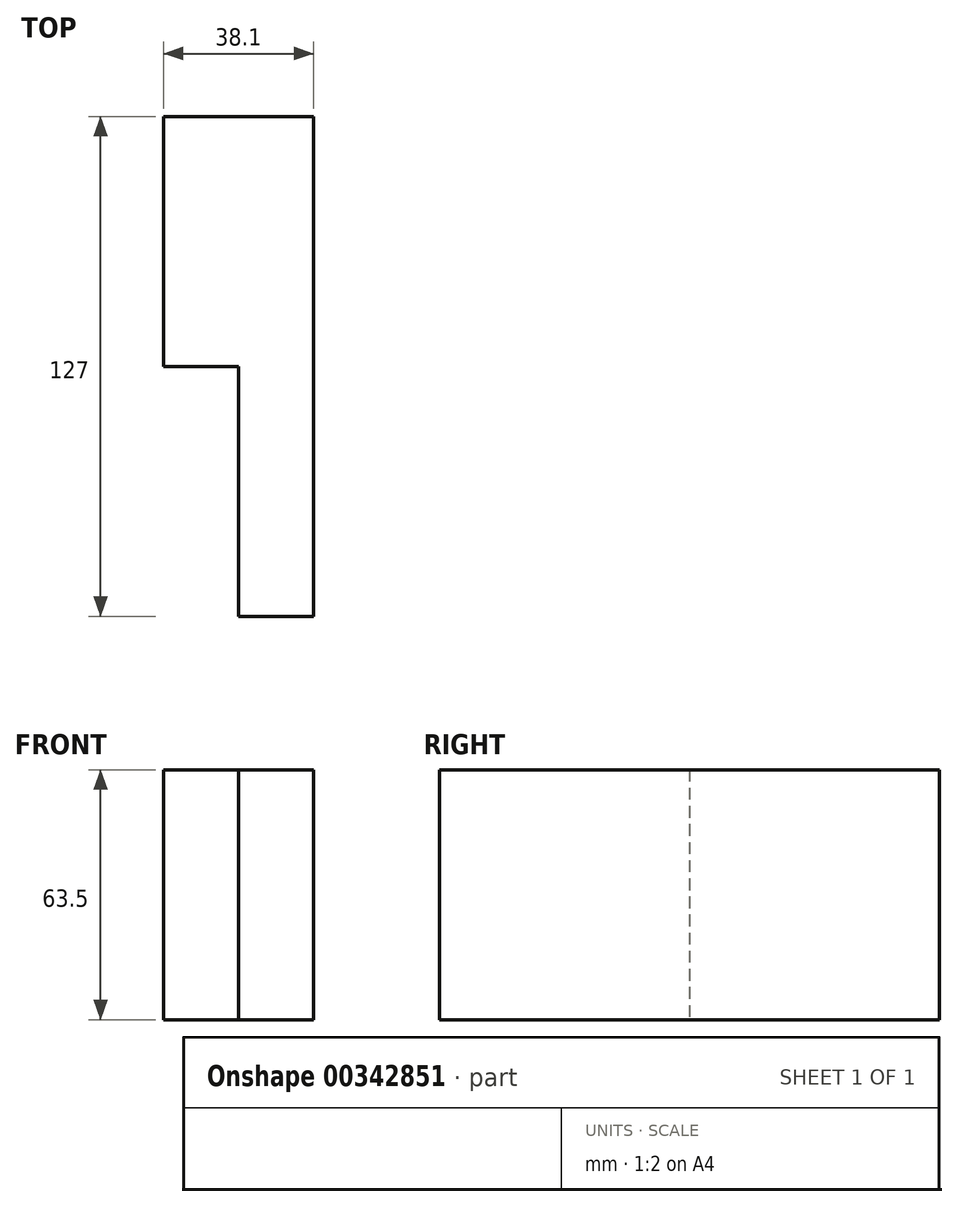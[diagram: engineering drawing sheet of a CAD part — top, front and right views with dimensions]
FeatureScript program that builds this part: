
annotation { "Feature Type Name" : "Feature", "Feature Type Description" : "" }
export const myFeature = defineFeature(function(context is Context, id is Id, definition is map)
    precondition{}
    {
        {
            var Q0;
            Q0=qCreatedBy(makeId("Top.planeOp"),FACE);
            var sketch = newSketch(context, id + "F0", { "sketchPlane" : qUnion([Q0])});
            skLineSegment(sketch, "E0.bottom", {"start": v(0, 73.15) * mm, "end": v(38.1, 73.15) * mm});
            skLineSegment(sketch, "E0.top", {"start": v(19.05, -53.85) * mm, "end": v(38.1, -53.85) * mm});
            skLineSegment(sketch, "E0.left", {"start": v(0, 73.15) * mm, "end": v(0, 9.65) * mm});
            skLineSegment(sketch, "E0.right", {"start": v(38.1, 73.15) * mm, "end": v(38.1, -53.85) * mm});
            skLineSegment(sketch, "E1", {"start": v(0, 9.65) * mm, "end": v(19.05, 9.65) * mm});
            skLineSegment(sketch, "E2", {"start": v(19.05, 9.65) * mm, "end": v(19.05, -53.85) * mm});
            skPoint(sketch, "E3.orphan", {"position": v(0, -53.85) * mm});
            skSolve(sketch);
        }
        {
            var Q0;
            Q0=makeQuery(id+"F0.imprint","IMPRINT",FACE,{"disambiguationData":[TD([[makeQuery(id+"F0.imprint","IMPRINT",EDGE,{"derivedFrom":sQuery(id+"F0.wireOp",EDGE,"E0.bottom")}),-1.0]])]});
            extrude(context, id + "F1", {"entities" : qUnion([Q0]), "depth" : 63.5 * mm});
        }
    });
